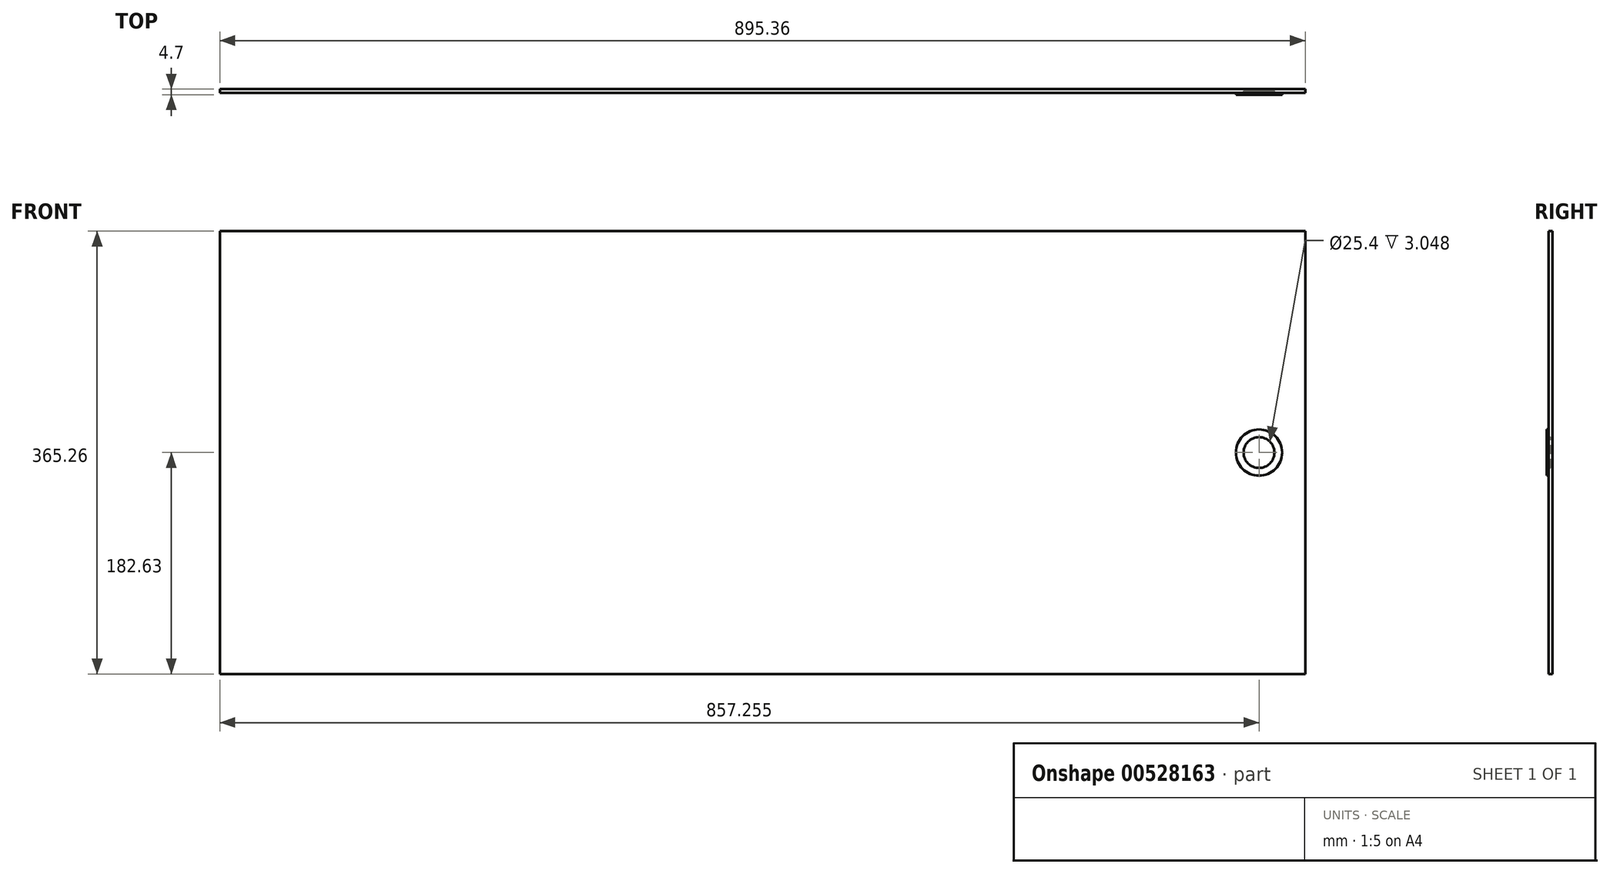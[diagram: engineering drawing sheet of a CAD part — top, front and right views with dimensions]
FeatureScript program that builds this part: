
annotation { "Feature Type Name" : "Feature", "Feature Type Description" : "" }
export const myFeature = defineFeature(function(context is Context, id is Id, definition is map)
    precondition{}
    {
        {
            var Q0;
            Q0=qCreatedBy(makeId("Front.planeOp"),FACE);
            var sketch = newSketch(context, id + "F0", { "sketchPlane" : qUnion([Q0])});
            skLineSegment(sketch, "E0.bottom", {"start": v(-447.68, 182.63) * mm, "end": v(447.68, 182.63) * mm});
            skLineSegment(sketch, "E0.top", {"start": v(-447.68, -182.63) * mm, "end": v(447.68, -182.63) * mm});
            skLineSegment(sketch, "E0.left", {"start": v(-447.68, 182.63) * mm, "end": v(-447.68, -182.63) * mm});
            skLineSegment(sketch, "E0.right", {"start": v(447.68, 182.63) * mm, "end": v(447.68, -182.63) * mm});
            skPoint(sketch, "E0.middle", {"position": v(0, 0) * mm});
            skSolve(sketch);
        }
        {
            var Q0;
            Q0=makeQuery(id+"F0.imprint","IMPRINT",FACE,{"disambiguationData":[TD([[makeQuery(id+"F0.imprint","IMPRINT",EDGE,{"derivedFrom":sQuery(id+"F0.wireOp",EDGE,"E0.bottom")}),-1.0]])]});
            extrude(context, id + "F1", {"entities" : qUnion([Q0]), "depth" : 3.17 * mm, "offsetDistance" : 25.4 * mm});
        }
        {
            var Q0;
            Q0=makeQuery(id+"F1.opExtrude","CAP_FACE",FACE,{"disambiguationData":[OSD([sQuery(id+"F0.wireOp",EDGE,"E0.bottom"),sQuery(id+"F0.wireOp",EDGE,"E0.top"),sQuery(id+"F0.wireOp",EDGE,"E0.left"),sQuery(id+"F0.wireOp",EDGE,"E0.right")])],"isStart":false});
            var sketch = newSketch(context, id + "F2", { "sketchPlane" : qUnion([Q0])});
            skLineSegment(sketch, "E1", {"start": v(447.68, 0) * mm, "end": v(409.58, 0) * mm});
            skCircle(sketch, "E2", {"center": v(409.58, 0) * mm, "radius": 19.05 * mm});
            skCircle(sketch, "E3", {"center": v(409.58, 0) * mm, "radius": 12.7 * mm});
            skSolve(sketch);
        }
        {
            var Q0;
            Q0=makeQuery(id+"F2.imprint","IMPRINT",FACE,{"disambiguationData":[TD([[makeQuery(id+"F2.imprint","IMPRINT",EDGE,{"derivedFrom":sQuery(id+"F2.wireOp",EDGE,"E2")}),1.0]])]});
            var Q1;
            Q1=sQuery(id+"F2.wireOp",EDGE,"E2");
            var Q2;
            Q2=sQuery(id+"F2.wireOp",EDGE,"E3");
            extrude(context, id + "F3", {"entities" : qUnion([Q0]), "operationType" : NewBodyOperationType.ADD, "surfaceEntities" : qUnion([Q1, Q2]), "depth" : 1.52 * mm, "offsetDistance" : 25.4 * mm});
        }
        {
            var Q0;
            Q0=makeQuery(id+"F3.boolean.opBoolean","SPLIT",FACE,{"disambiguationData":[TD([makeQuery(id+"F3.opExtrude","SWEPT_FACE",FACE,{"disambiguationData":[OSD([sQuery(id+"F2.wireOp",EDGE,"E3")])]})])],"derivedFrom":makeQuery(id+"F1.opExtrude","CAP_FACE",FACE,{"disambiguationData":[OSD([sQuery(id+"F0.wireOp",EDGE,"E0.bottom"),sQuery(id+"F0.wireOp",EDGE,"E0.top"),sQuery(id+"F0.wireOp",EDGE,"E0.left"),sQuery(id+"F0.wireOp",EDGE,"E0.right")])],"isStart":false})});
            extrude(context, id + "F4", {"entities" : qUnion([Q0]), "operationType" : NewBodyOperationType.REMOVE, "oppositeDirection" : true, "depth" : 1.52 * mm, "offsetDistance" : 25.4 * mm});
        }
    });
